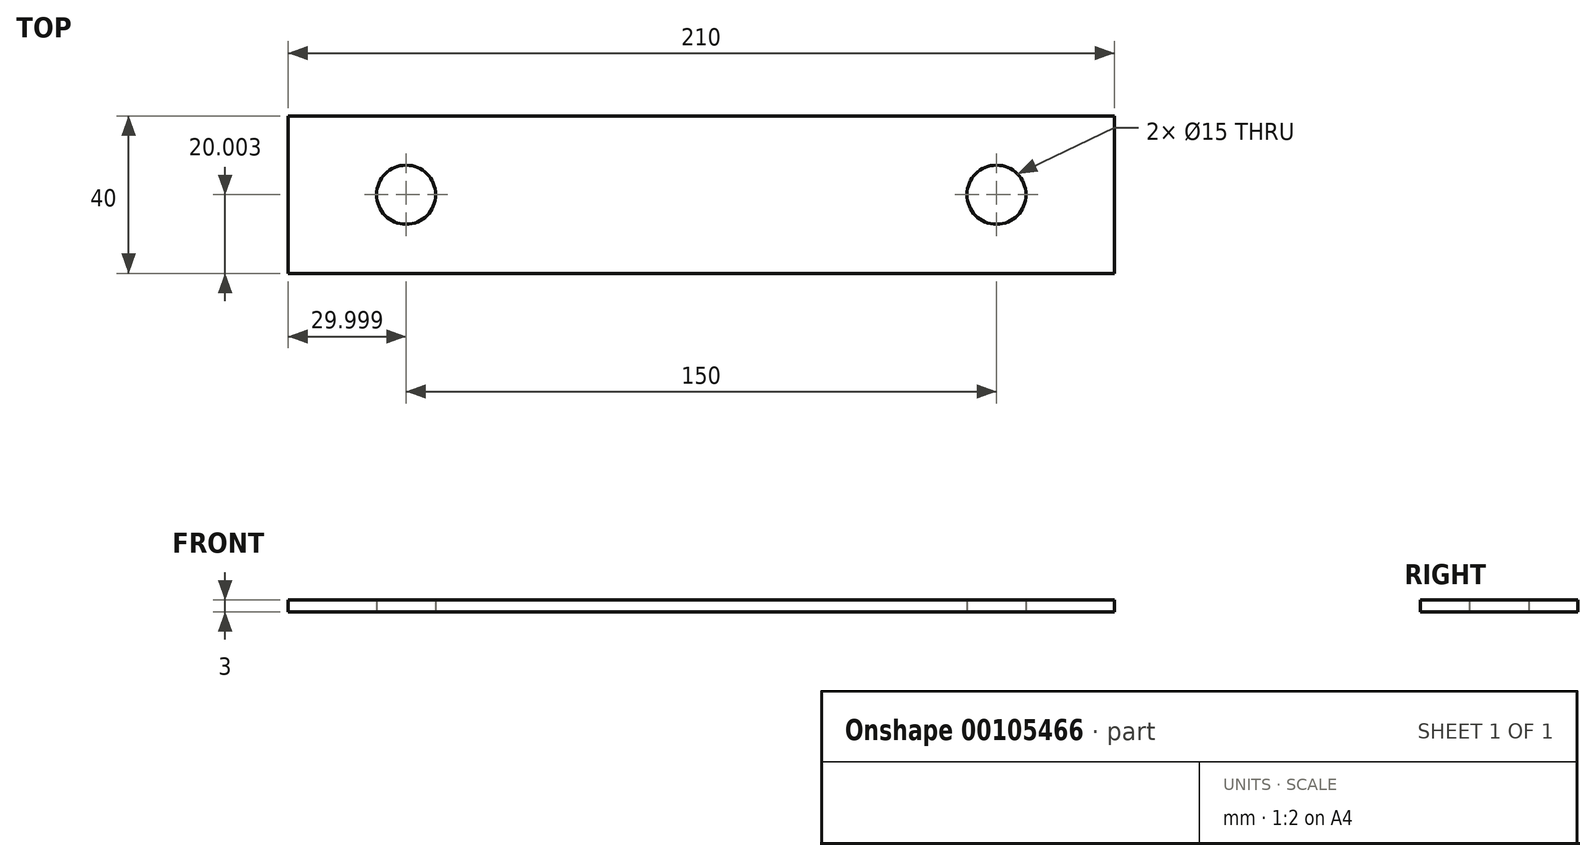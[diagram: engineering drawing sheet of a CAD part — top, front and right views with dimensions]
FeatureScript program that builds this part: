
annotation { "Feature Type Name" : "Feature", "Feature Type Description" : "" }
export const myFeature = defineFeature(function(context is Context, id is Id, definition is map)
    precondition{}
    {
        {
            var Q0;
            Q0=qCreatedBy(makeId("Top.planeOp"),FACE);
            var sketch = newSketch(context, id + "F0", { "sketchPlane" : qUnion([Q0])});
            skLineSegment(sketch, "E0.bottom", {"start": v(-117.51, 29.2) * mm, "end": v(92.49, 29.2) * mm});
            skLineSegment(sketch, "E0.top", {"start": v(-117.51, -10.8) * mm, "end": v(92.49, -10.8) * mm});
            skLineSegment(sketch, "E0.left", {"start": v(-117.51, 29.2) * mm, "end": v(-117.51, -10.8) * mm});
            skLineSegment(sketch, "E0.right", {"start": v(92.49, 29.2) * mm, "end": v(92.49, -10.8) * mm});
            skCircle(sketch, "E1", {"center": v(-87.51, 9.2) * mm, "radius": 7.5 * mm});
            skCircle(sketch, "E2", {"center": v(62.49, 9.2) * mm, "radius": 7.5 * mm});
            skSolve(sketch);
        }
        {
            var Q0;
            Q0 = qSketchRegion(id + "F0", true);
            extrude(context, id + "F1", {"entities" : qUnion([Q0]), "depth" : 3 * mm});
        }
    });
